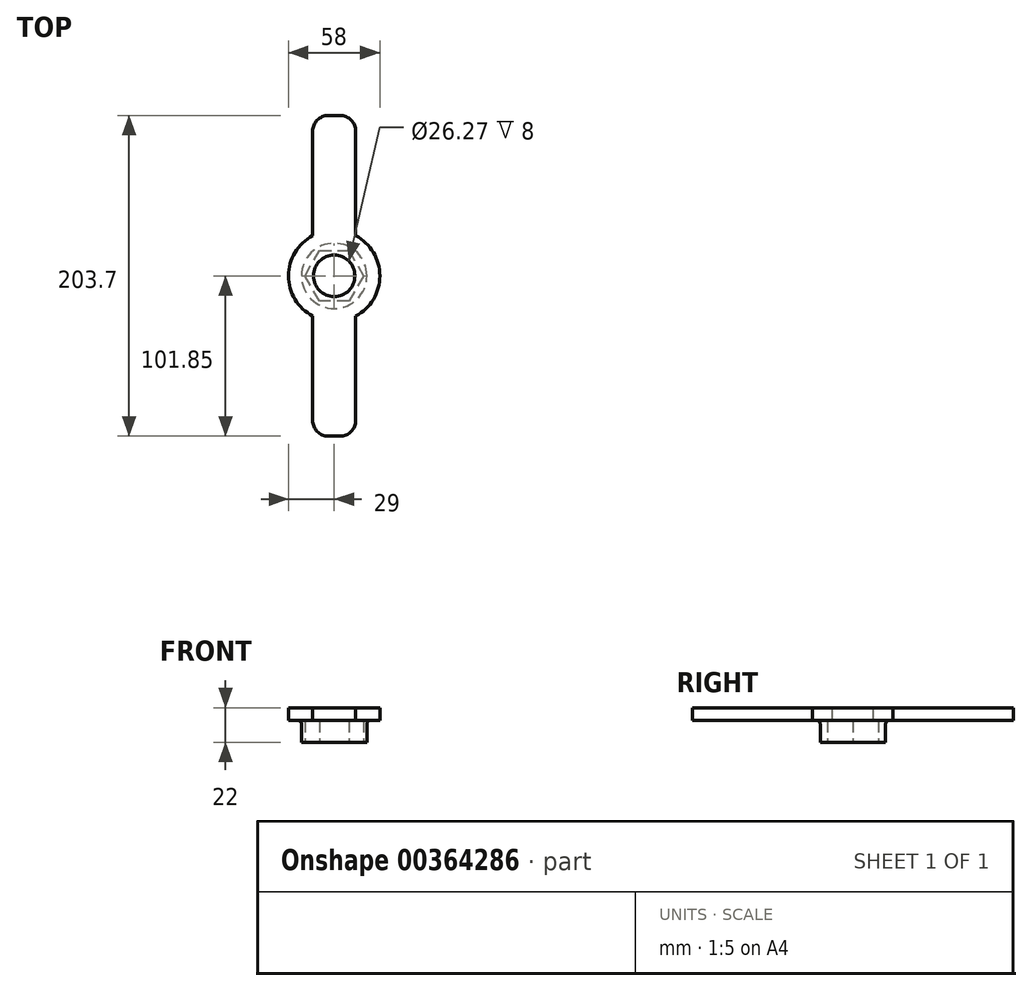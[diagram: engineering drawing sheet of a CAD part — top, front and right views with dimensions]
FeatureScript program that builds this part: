
annotation { "Feature Type Name" : "Feature", "Feature Type Description" : "" }
export const myFeature = defineFeature(function(context is Context, id is Id, definition is map)
    precondition{}
    {
        {
            var Q0;
            Q0=qCreatedBy(makeId("Top.planeOp"),FACE);
            var sketch = newSketch(context, id + "F0", { "sketchPlane" : qUnion([Q0])});
            skCircle(sketch, "E0.cCircle", {"center": v(0, 0) * mm, "radius": 16.12 * mm, "construction": true});
            skLineSegment(sketch, "E0.0", {"start": v(-9.3, 16.12) * mm, "end": v(9.3, 16.12) * mm});
            skLineSegment(sketch, "E0.1", {"start": v(9.3, 16.12) * mm, "end": v(18.62, 0) * mm});
            skLineSegment(sketch, "E0.2", {"start": v(18.62, 0) * mm, "end": v(9.3, -16.12) * mm});
            skLineSegment(sketch, "E0.3", {"start": v(9.3, -16.12) * mm, "end": v(-9.3, -16.12) * mm});
            skLineSegment(sketch, "E0.4", {"start": v(-9.3, -16.13) * mm, "end": v(-18.62, 0) * mm});
            skLineSegment(sketch, "E0.5", {"start": v(-18.62, 0) * mm, "end": v(-9.3, 16.12) * mm});
            skPoint(sketch, "E0.0.midPoint", {"position": v(0, 16.12) * mm});
            skCircle(sketch, "E1", {"center": v(0, 0) * mm, "radius": 20.75 * mm});
            skSolve(sketch);
        }
        {
            var Q0;
            Q0 = qSketchRegion(id + "F0", true);
            extrude(context, id + "F1", {"entities" : qUnion([Q0]), "depth" : 14 * mm});
        }
        {
            var Q0;
            Q0=makeQuery(id+"F1.opExtrude","CAP_FACE",FACE,{"disambiguationData":[OSD([sQuery(id+"F0.wireOp",EDGE,"E0.0"),sQuery(id+"F0.wireOp",EDGE,"E0.1"),sQuery(id+"F0.wireOp",EDGE,"E0.2"),sQuery(id+"F0.wireOp",EDGE,"E0.3"),sQuery(id+"F0.wireOp",EDGE,"E0.4"),sQuery(id+"F0.wireOp",EDGE,"E0.5"),sQuery(id+"F0.wireOp",EDGE,"E1")])],"isStart":false});
            var sketch = newSketch(context, id + "F2", { "sketchPlane" : qUnion([Q0])});
            skArc(sketch, "E2", {"start": v(-13.7, 25.56) * mm, "mid": v(-29, 0) * mm, "end": v(-13.7, -25.56) * mm});
            skLineSegment(sketch, "E3.bottom", {"start": v(3.7, 101.85) * mm, "end": v(-3.7, 101.85) * mm});
            skLineSegment(sketch, "E3.top", {"start": v(3.7, -101.85) * mm, "end": v(-3.7, -101.85) * mm});
            skLineSegment(sketch, "E3.left", {"start": v(13.7, 91.85) * mm, "end": v(13.7, 25.56) * mm});
            skLineSegment(sketch, "E3.right", {"start": v(-13.7, 91.85) * mm, "end": v(-13.7, 25.56) * mm});
            skPoint(sketch, "E4.visualSharp", {"position": v(-13.7, 101.85) * mm});
            skArc(sketch, "E4.filletArc", {"start": v(-3.7, 101.85) * mm, "mid": v(-10.77, 98.92) * mm, "end": v(-13.7, 91.85) * mm});
            skPoint(sketch, "E5.visualSharp", {"position": v(13.7, 101.85) * mm});
            skArc(sketch, "E5.filletArc", {"start": v(13.7, 91.85) * mm, "mid": v(10.77, 98.92) * mm, "end": v(3.7, 101.85) * mm});
            skPoint(sketch, "E6.visualSharp", {"position": v(-13.7, -101.85) * mm});
            skArc(sketch, "E6.filletArc", {"start": v(-13.7, -91.85) * mm, "mid": v(-10.77, -98.92) * mm, "end": v(-3.7, -101.85) * mm});
            skPoint(sketch, "E7.visualSharp", {"position": v(13.7, -101.85) * mm});
            skArc(sketch, "E7.filletArc", {"start": v(3.7, -101.85) * mm, "mid": v(10.77, -98.92) * mm, "end": v(13.7, -91.85) * mm});
            skLineSegment(sketch, "E8.trimOffspring", {"start": v(-13.7, -25.56) * mm, "end": v(-13.7, -91.85) * mm});
            skLineSegment(sketch, "E9.trimOffspring", {"start": v(13.7, -25.56) * mm, "end": v(13.7, -91.85) * mm});
            skArc(sketch, "E10.trimOffspring", {"start": v(13.7, -25.56) * mm, "mid": v(29, 0) * mm, "end": v(13.7, 25.56) * mm});
            skSolve(sketch);
        }
        {
            var Q0;
            Q0 = qSketchRegion(id + "F2", true);
            extrude(context, id + "F3", {"entities" : qUnion([Q0]), "operationType" : NewBodyOperationType.ADD, "depth" : 8 * mm});
        }
        {
            var Q0;
            Q0=makeQuery(id+"F3.opExtrude","CAP_FACE",FACE,{"disambiguationData":[OSD([sQuery(id+"F2.wireOp",EDGE,"E2"),sQuery(id+"F2.wireOp",EDGE,"E3.bottom"),sQuery(id+"F2.wireOp",EDGE,"E3.top"),sQuery(id+"F2.wireOp",EDGE,"E3.left"),sQuery(id+"F2.wireOp",EDGE,"E3.right"),sQuery(id+"F2.wireOp",EDGE,"E4.filletArc"),sQuery(id+"F2.wireOp",EDGE,"E5.filletArc"),sQuery(id+"F2.wireOp",EDGE,"E6.filletArc"),sQuery(id+"F2.wireOp",EDGE,"E7.filletArc"),sQuery(id+"F2.wireOp",EDGE,"E8.trimOffspring"),sQuery(id+"F2.wireOp",EDGE,"E9.trimOffspring"),sQuery(id+"F2.wireOp",EDGE,"E10.trimOffspring")])],"isStart":false});
            var sketch = newSketch(context, id + "F4", { "sketchPlane" : qUnion([Q0])});
            skCircle(sketch, "E11", {"center": v(0, 0) * mm, "radius": 13.13 * mm});
            skSolve(sketch);
        }
        {
            var Q0;
            Q0 = qSketchRegion(id + "F4", true);
            extrude(context, id + "F5", {"entities" : qUnion([Q0]), "operationType" : NewBodyOperationType.REMOVE, "oppositeDirection" : true, "depth" : 25 * mm});
        }
        {
            var Q0;
            Q0=makeQuery(id+"F1.opExtrude","CAP_EDGE",EDGE,{"disambiguationData":[OSD([sQuery(id+"F0.wireOp",EDGE,"E0.0")])],"isStart":false});
            var Q1;
            Q1=makeQuery(id+"F1.opExtrude","CAP_EDGE",EDGE,{"disambiguationData":[OSD([sQuery(id+"F0.wireOp",EDGE,"E0.5")])],"isStart":false});
            var Q2;
            Q2=makeQuery(id+"F1.opExtrude","CAP_EDGE",EDGE,{"disambiguationData":[OSD([sQuery(id+"F0.wireOp",EDGE,"E0.4")])],"isStart":false});
            var Q3;
            Q3=makeQuery(id+"F1.opExtrude","CAP_EDGE",EDGE,{"disambiguationData":[OSD([sQuery(id+"F0.wireOp",EDGE,"E0.3")])],"isStart":false});
            var Q4;
            Q4=makeQuery(id+"F1.opExtrude","CAP_EDGE",EDGE,{"disambiguationData":[OSD([sQuery(id+"F0.wireOp",EDGE,"E0.2")])],"isStart":false});
            var Q5;
            Q5=makeQuery(id+"F1.opExtrude","CAP_EDGE",EDGE,{"disambiguationData":[OSD([sQuery(id+"F0.wireOp",EDGE,"E0.1")])],"isStart":false});
            var Q6;
            Q6=makeQuery(id+"F1.opExtrude","CAP_EDGE",EDGE,{"disambiguationData":[OSD([sQuery(id+"F0.wireOp",EDGE,"E1")])],"isStart":false});
            fillet(context, id + "F6", {"entities" : qUnion([Q0, Q1, Q2, Q3, Q4, Q5, Q6]), "radius" : 2.5 * mm, "tangentPropagation" : true, "allowEdgeOverflow" : false});
        }
    });
